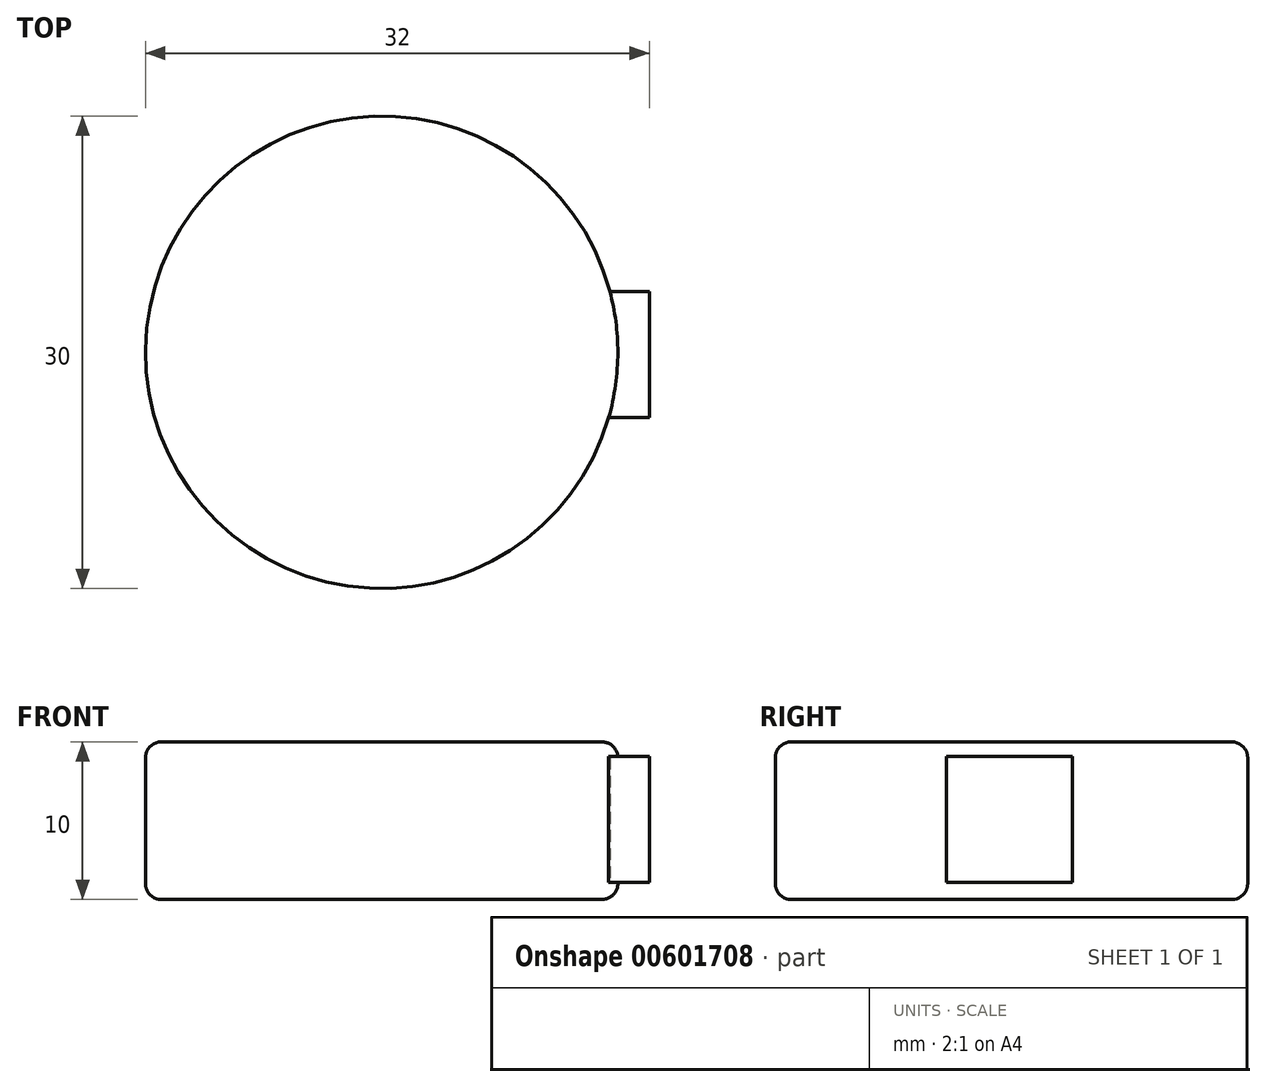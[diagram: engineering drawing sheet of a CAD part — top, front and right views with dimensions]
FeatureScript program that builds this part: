
annotation { "Feature Type Name" : "Feature", "Feature Type Description" : "" }
export const myFeature = defineFeature(function(context is Context, id is Id, definition is map)
    precondition{}
    {
        {
            var Q0;
            Q0=qCreatedBy(makeId("Top.planeOp"),FACE);
            var sketch = newSketch(context, id + "F0", { "sketchPlane" : qUnion([Q0])});
            skCircle(sketch, "E0", {"center": v(0, 0) * mm, "radius": 15 * mm});
            skSolve(sketch);
        }
        {
            var Q0;
            Q0=makeQuery(id+"F0.imprint","IMPRINT",FACE,{"disambiguationData":[TD([[makeQuery(id+"F0.imprint","IMPRINT",EDGE,{"derivedFrom":sQuery(id+"F0.wireOp",EDGE,"E0")}),1.0]])]});
            extrude(context, id + "F1", {"entities" : qUnion([Q0]), "depth" : 10 * mm, "offsetDistance" : 25 * mm});
        }
        {
            var Q0;
            Q0=qCreatedBy(makeId("Right.planeOp"),FACE);
            var sketch = newSketch(context, id + "F2", { "sketchPlane" : qUnion([Q0])});
            skLineSegment(sketch, "E1.bottom", {"start": v(3.87, 9.07) * mm, "end": v(-4.13, 9.07) * mm});
            skLineSegment(sketch, "E1.top", {"start": v(3.87, 1.07) * mm, "end": v(-4.13, 1.07) * mm});
            skLineSegment(sketch, "E1.left", {"start": v(3.87, 9.07) * mm, "end": v(3.87, 1.07) * mm});
            skLineSegment(sketch, "E1.right", {"start": v(-4.13, 9.07) * mm, "end": v(-4.13, 1.07) * mm});
            skSolve(sketch);
        }
        {
            var Q0;
            Q0 = qSketchRegion(id + "F2", true);
            extrude(context, id + "F3", {"entities" : qUnion([Q0]), "operationType" : NewBodyOperationType.ADD, "depth" : 17 * mm, "offsetDistance" : 25 * mm});
        }
        {
            var Q0;
            Q0=makeQuery(id+"F1.opExtrude","CAP_EDGE",EDGE,{"disambiguationData":[OSD([sQuery(id+"F0.wireOp",EDGE,"E0")])],"isStart":false});
            var Q1;
            Q1=makeQuery(id+"F1.opExtrude","CAP_EDGE",EDGE,{"disambiguationData":[OSD([sQuery(id+"F0.wireOp",EDGE,"E0")])],"isStart":true});
            fillet(context, id + "F4", {"entities" : qUnion([Q0, Q1]), "radius" : 1 * mm, "tangentPropagation" : true, "allowEdgeOverflow" : false});
        }
    });
